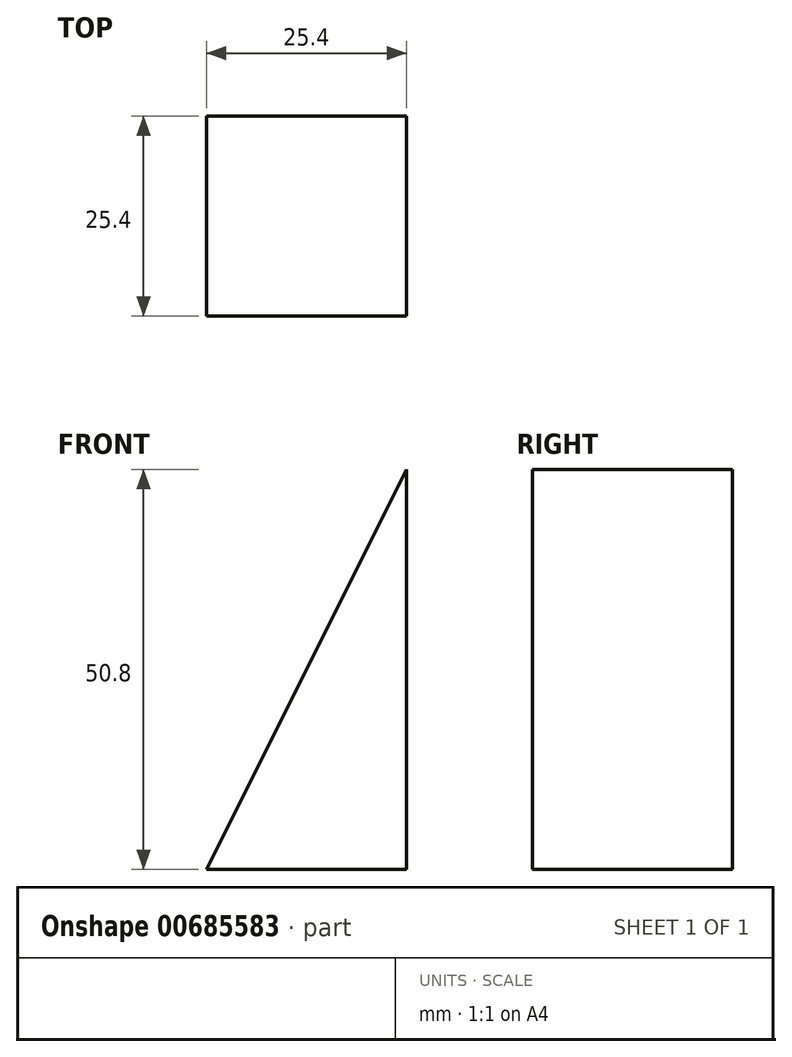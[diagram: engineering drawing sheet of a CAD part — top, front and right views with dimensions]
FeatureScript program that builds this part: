
annotation { "Feature Type Name" : "Feature", "Feature Type Description" : "" }
export const myFeature = defineFeature(function(context is Context, id is Id, definition is map)
    precondition{}
    {
        {
            var Q0;
            Q0=qCreatedBy(makeId("Front.planeOp"),FACE);
            var sketch = newSketch(context, id + "F0", { "sketchPlane" : qUnion([Q0])});
            skLineSegment(sketch, "E0", {"start": v(0, 0) * mm, "end": v(-25.4, 0) * mm});
            skLineSegment(sketch, "E1", {"start": v(-25.4, 0) * mm, "end": v(0, 50.8) * mm});
            skLineSegment(sketch, "E2", {"start": v(0, 50.8) * mm, "end": v(0, 0) * mm});
            skSolve(sketch);
        }
        {
            var Q0;
            Q0 = qSketchRegion(id + "F0", true);
            extrude(context, id + "F1", {"entities" : qUnion([Q0]), "depth" : 25.4 * mm, "offsetDistance" : 25.4 * mm});
        }
    });
